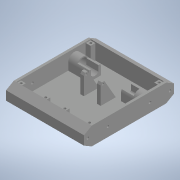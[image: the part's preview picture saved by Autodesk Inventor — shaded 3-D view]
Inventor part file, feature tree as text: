
AUTODESK INVENTOR PART (.ipt)
format: ipt  version: 2020 (Build 240168000, 168)  size: 390,656 bytes
history: native  units: in
note: dims shown in document units (in); Inventor stores cm internally (conversion verified against a paired STEP export)
features: projected_geometry x13, extrude x11, sketch x11, mirror x4, plane x1
ambient origin geometry x8: Origin, YZ Plane, XZ Plane, XY Plane, X Axis, Y Axis, Z Axis, Center Point
bodies: Solid1 (feature_tree)
feature tree (40):
  extrude  "Extrusion1"  Depth=5.9055in
  extrude  "Extrusion2"  TaperAngle=0.0deg  [1 undecoded]
  extrude  "Extrusion3"  Depth=1.063in
  extrude  "Extrusion4"  Depth=0.315in
  extrude  "Extrusion5"  TaperAngle=0.0deg  [1 undecoded]
  extrude  "Extrusion6"  Depth=0.5906in
  mirror  "Mirror1"
  extrude  "Extrusion7"  Depth=0.0787in
  mirror  "Mirror2"
  extrude  "Extrusion8"  Depth=0.5512in
  mirror  "Mirror3"
  plane  "Work Plane1"
  extrude  "Extrusion9"  Depth=0.7874in TaperAngle=0.0deg
  mirror  "Mirror4"
  extrude  "Extrusion10"  Depth=6.063in TaperAngle=0.0deg
  extrude  "Extrusion11"  Depth=0.1575in
  sketch  "Sketch1"  dims[d0=1.1811in d1=5.9055in]
  sketch  "Sketch2"  dims[d2=5.1181in d3=0.0in]
  projected_geometry  "Projected Loop1"
  sketch  "Sketch3"  dims[d4=0.1575in d5=1.063in]
  projected_geometry  "Projected Loop2"
  projected_geometry  "Projected Loop3"
  sketch  "Sketch4"  dims[d6=0.0in d8=0.315in]
  sketch  "Sketch5"  dims[d10=0.993in d11=0.0in]
  projected_geometry  "Projected Loop4"
  sketch  "Sketch6"  dims[d12=0.6496in d13=0.5906in]
  sketch  "Sketch7"  dims[d14=1.5748in d15=0.0787in]
  sketch  "Sketch9"  dims[d16=0.5512in d17=0.0in d18=0.6102in]
  sketch  "Sketch10"  dims[d19=0.4803in d20=0.7874in d21=0.0in]
  sketch  "Sketch12"  dims[d22=0.1654in d23=6.063in d24=0.0in]
  projected_geometry  "Projected Loop6"
  projected_geometry  "Projected Loop7"
  projected_geometry  "Projected Loop8"
  sketch  "Sketch13"  dims[d25=0.5114in d26=0.1575in d27=1.5748in d28=0.0in d29=0.0in d30=0.1575in d31=0.2756in d32=0.0in d33=0.4331in d34=0.122in d38=2.7559in d40=0.061in d41=0.0909in d42=0.2362in d43=0.0in d44=60.0deg d45=0.0787in d46=0.315in d48=0.993in d49=0.0in d51=0.1575in d52=0.1575in d53=0.2756in d54=0.0in d55=0.4724in]
  projected_geometry  "Projected Loop9"
  projected_geometry  "Projected Loop10"
  projected_geometry  "Projected Loop11"
  projected_geometry  "Projected Loop12"
  projected_geometry  "Projected Loop13"
  projected_geometry  "Projected Loop14"
note: 2 required parameter values undecoded (feature->parameter linkage not recoverable at this tier; creation-order binding heuristic only, values carry confidence <= 0.55)
